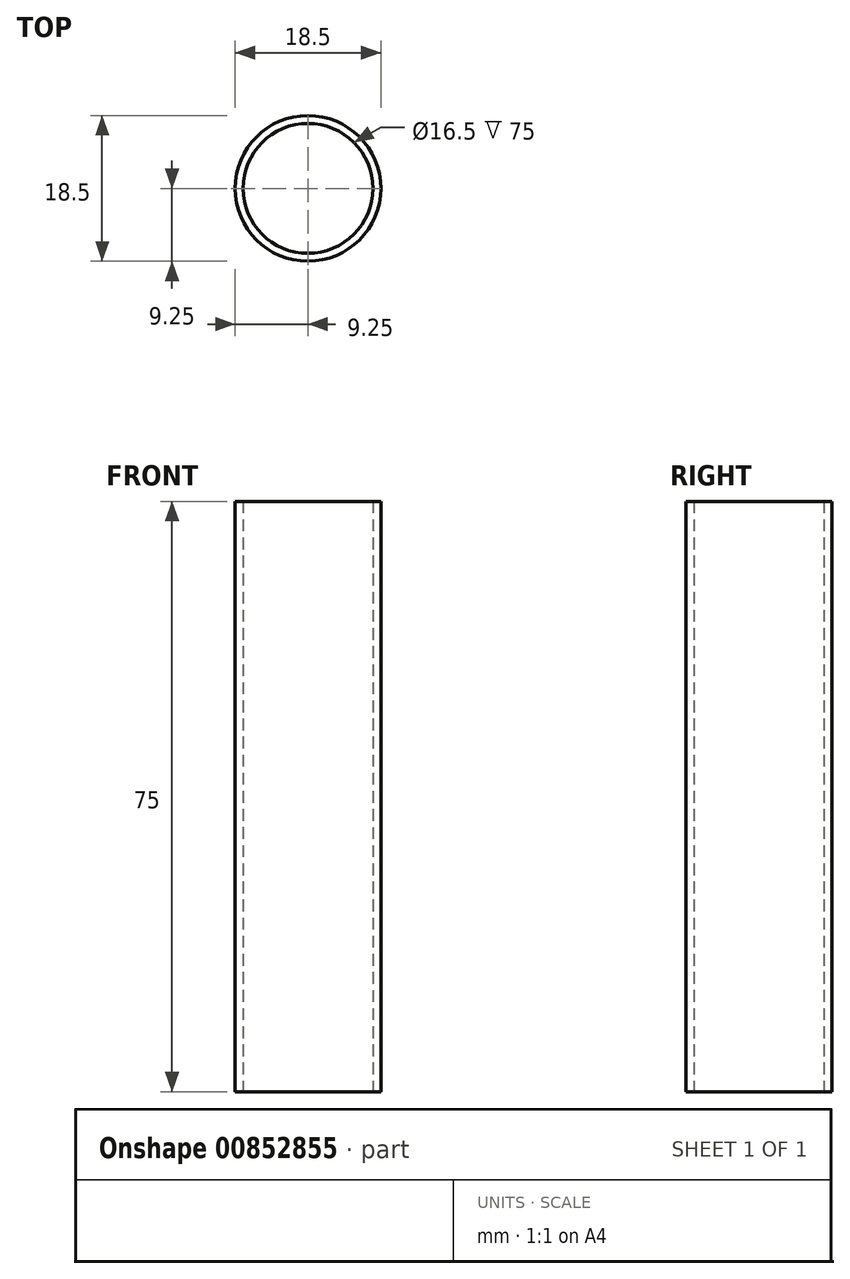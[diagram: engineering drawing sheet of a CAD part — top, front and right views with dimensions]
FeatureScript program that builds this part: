
annotation { "Feature Type Name" : "Feature", "Feature Type Description" : "" }
export const myFeature = defineFeature(function(context is Context, id is Id, definition is map)
    precondition{}
    {
        {
            var Q0;
            Q0=qCreatedBy(makeId("Top.planeOp"),FACE);
            var sketch = newSketch(context, id + "F0", { "sketchPlane" : qUnion([Q0])});
            skCircle(sketch, "E0", {"center": v(0, 0) * mm, "radius": 9.25 * mm});
            skCircle(sketch, "E1", {"center": v(0, 0) * mm, "radius": 8.25 * mm});
            skSolve(sketch);
        }
        {
            var Q0;
            Q0=makeQuery(id+"F0.imprint","IMPRINT",FACE,{"disambiguationData":[TD([[makeQuery(id+"F0.imprint","IMPRINT",EDGE,{"derivedFrom":sQuery(id+"F0.wireOp",EDGE,"E0")}),1.0]])]});
            extrude(context, id + "F1", {"entities" : qUnion([Q0]), "depth" : 75 * mm, "offsetDistance" : 25 * mm});
        }
    });
